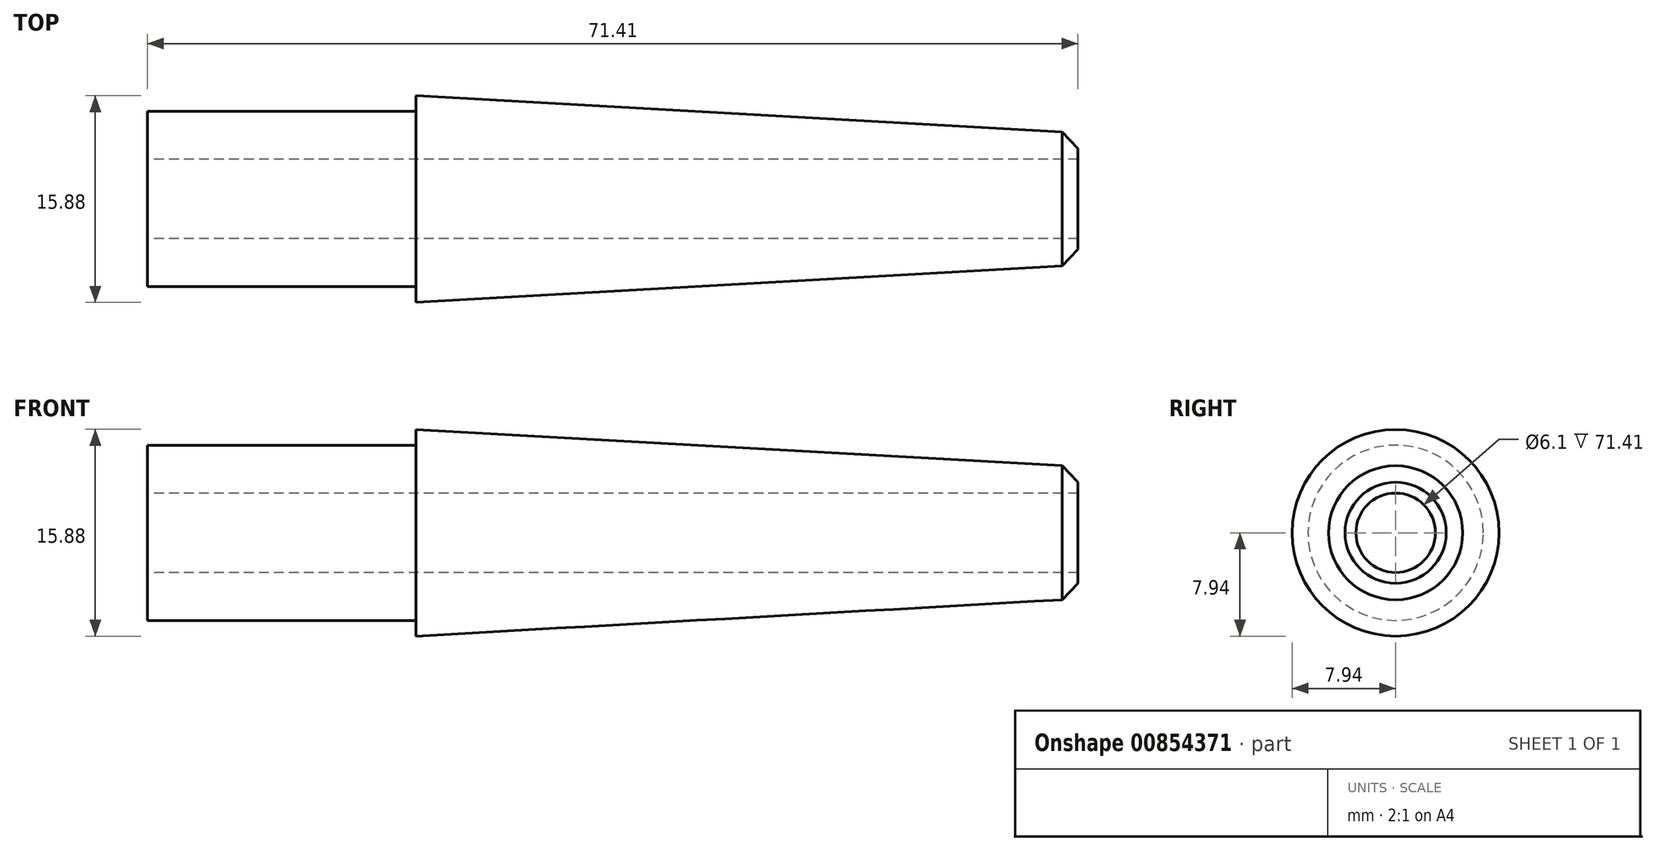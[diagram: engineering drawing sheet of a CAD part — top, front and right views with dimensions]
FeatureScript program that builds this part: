
annotation { "Feature Type Name" : "Feature", "Feature Type Description" : "" }
export const myFeature = defineFeature(function(context is Context, id is Id, definition is map)
    precondition{}
    {
        {
            var Q0;
            Q0=qCreatedBy(makeId("Front.planeOp"),FACE);
            var sketch = newSketch(context, id + "F0", { "sketchPlane" : qUnion([Q0])});
            skLineSegment(sketch, "E0", {"start": v(0, 7.94) * mm, "end": v(50.8, 5.08) * mm});
            skLineSegment(sketch, "E1", {"start": v(50.8, 5.08) * mm, "end": v(50.8, 0) * mm});
            skLineSegment(sketch, "E2", {"start": v(50.8, 0) * mm, "end": v(0, 0) * mm});
            skLineSegment(sketch, "E3", {"start": v(0, 7.94) * mm, "end": v(0, 6.73) * mm});
            skLineSegment(sketch, "E4", {"start": v(0, 6.73) * mm, "end": v(-20.6, 6.73) * mm});
            skLineSegment(sketch, "E5", {"start": v(-20.6, 6.73) * mm, "end": v(-20.6, 0) * mm});
            skLineSegment(sketch, "E6", {"start": v(-20.6, 0) * mm, "end": v(0, 0) * mm});
            skSolve(sketch);
        }
        {
            var Q0;
            Q0=makeQuery(id+"F0.imprint","IMPRINT",FACE,{"disambiguationData":[TD([[makeQuery(id+"F0.imprint","IMPRINT",EDGE,{"derivedFrom":sQuery(id+"F0.wireOp",EDGE,"E0")}),-1.0]])]});
            var Q1;
            Q1=sQuery(id+"F0.wireOp",EDGE,"E2");
            revolve(context, id + "F1", {"surfaceOperationType" : NewSurfaceOperationType.NEW, "entities" : qUnion([Q0]), "axis" : qUnion([Q1]), "revolveType" : RevolveType.FULL});
        }
        {
            var Q0;
            Q0=qCreatedBy(makeId("Right.planeOp"),FACE);
            var sketch = newSketch(context, id + "F2", { "sketchPlane" : qUnion([Q0])});
            skCircle(sketch, "E7", {"center": v(0, 0) * mm, "radius": 3.05 * mm});
            skSolve(sketch);
        }
        {
            var Q0;
            Q0=makeQuery(id+"F2.imprint","IMPRINT",FACE,{"disambiguationData":[TD([[makeQuery(id+"F2.imprint","IMPRINT",EDGE,{"derivedFrom":sQuery(id+"F2.wireOp",EDGE,"E7")}),1.0]])]});
            var Q1;
            Q1=sQuery(id+"F2.wireOp",EDGE,"E7");
            extrude(context, id + "F3", {"entities" : qUnion([Q0]), "operationType" : NewBodyOperationType.REMOVE, "surfaceEntities" : qUnion([Q1]), "depth" : 76.2 * mm, "offsetDistance" : 25.4 * mm, "hasSecondDirection" : true, "secondDirectionOppositeDirection" : true, "secondDirectionDepth" : 76.2 * mm});
        }
        {
            var Q0;
            Q0=makeQuery(id+"F1.opRevolve","SWEPT_EDGE",EDGE,{"disambiguationData":[OSD([sQuery(id+"F0.wireOp",EDGE,"E0"),sQuery(id+"F0.wireOp",EDGE,"E1")])]});
            chamfer(context, id + "F4", {"entities" : qUnion([Q0]), "width" : 1.27 * mm, "tangentPropagation" : true});
        }
    });
